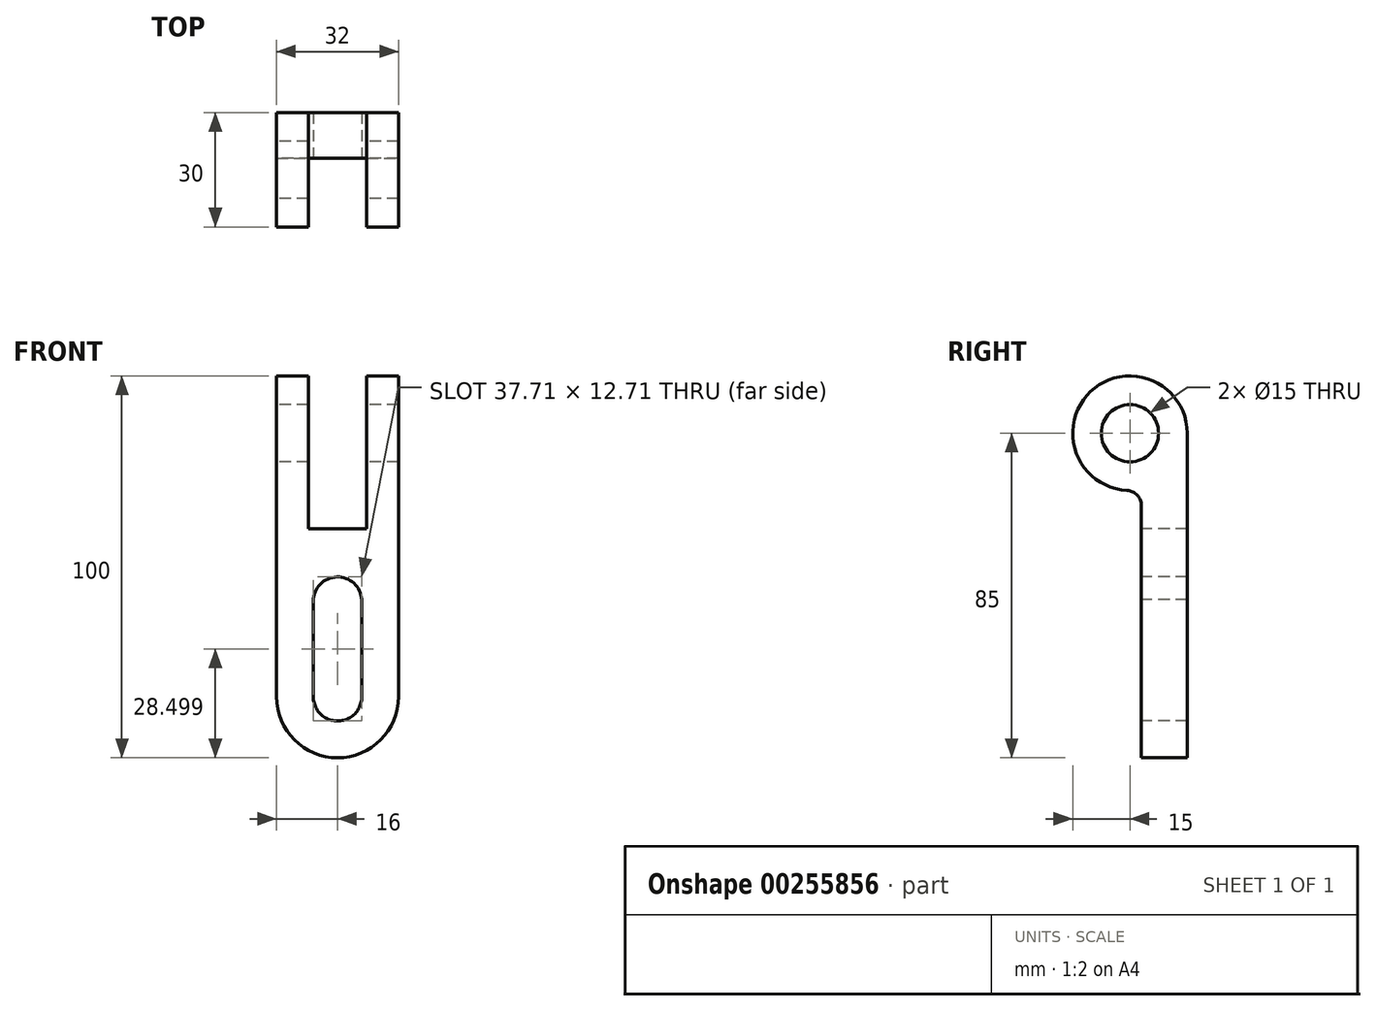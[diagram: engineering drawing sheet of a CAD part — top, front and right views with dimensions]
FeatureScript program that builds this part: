
annotation { "Feature Type Name" : "Feature", "Feature Type Description" : "" }
export const myFeature = defineFeature(function(context is Context, id is Id, definition is map)
    precondition{}
    {
        {
            var Q0;
            Q0=qCreatedBy(makeId("Right.planeOp"),FACE);
            var sketch = newSketch(context, id + "F0", { "sketchPlane" : qUnion([Q0])});
            skCircle(sketch, "E0", {"center": v(0, 0) * mm, "radius": 7.5 * mm});
            skArc(sketch, "E1", {"start": v(15, 0) * mm, "mid": v(-11.62, 9.49) * mm, "end": v(3, -14.7) * mm});
            skLineSegment(sketch, "E2.top", {"start": v(15, -85) * mm, "end": v(3, -85) * mm});
            skLineSegment(sketch, "E2.left", {"start": v(15, 0) * mm, "end": v(15, -85) * mm});
            skLineSegment(sketch, "E2.right", {"start": v(3, -14.7) * mm, "end": v(3, -85) * mm});
            skSolve(sketch);
        }
        {
            var Q0;
            Q0=makeQuery(id+"F0.imprint","IMPRINT",FACE,{"disambiguationData":[TD([[makeQuery(id+"F0.imprint","IMPRINT",EDGE,{"derivedFrom":sQuery(id+"F0.wireOp",EDGE,"E0")}),-1.0]])]});
            extrude(context, id + "F1", {"entities" : qUnion([Q0]), "endBound" : BoundingType.SYMMETRIC, "depth" : 32 * mm});
        }
        {
            var Q0;
            Q0=qCreatedBy(makeId("Front.planeOp"),FACE);
            cPlane(context, id + "F2", {"entities" : qUnion([Q0]), "cplaneType" : CPlaneType.OFFSET, "offset" : 40.5 * mm, "width" : 150 * mm, "height" : 150 * mm});
        }
        {
            var Q0;
            Q0=qCreatedBy(id+"F2.planeOp",FACE);
            var sketch = newSketch(context, id + "F3", { "sketchPlane" : qUnion([Q0])});
            skLineSegment(sketch, "E3.0", {"start": v(16, 15) * mm, "end": v(16, -15) * mm});
            skLineSegment(sketch, "E4.0", {"start": v(-16, 15) * mm, "end": v(-16, -15) * mm});
            skLineSegment(sketch, "E5.0.0", {"start": v(-16, -14.7) * mm, "end": v(-16, -85) * mm});
            skLineSegment(sketch, "E5.0.2", {"start": v(16, -85) * mm, "end": v(16, -14.7) * mm});
            skLineSegment(sketch, "E6.bottom", {"start": v(7.65, -25) * mm, "end": v(-7.65, -25) * mm});
            skLineSegment(sketch, "E6.top", {"start": v(7.65, 25) * mm, "end": v(-7.65, 25) * mm});
            skLineSegment(sketch, "E6.left", {"start": v(7.65, -25) * mm, "end": v(7.65, 25) * mm});
            skLineSegment(sketch, "E6.right", {"start": v(-7.65, -25) * mm, "end": v(-7.65, 25) * mm});
            skPoint(sketch, "E6.middle", {"position": v(0, 0) * mm});
            skArc(sketch, "E7", {"start": v(6.35, -44.37) * mm, "mid": v(0.19, -37.65) * mm, "end": v(-6.36, -44) * mm});
            skArc(sketch, "E8", {"start": v(-6.36, -69) * mm, "mid": v(0, -75.36) * mm, "end": v(6.36, -69) * mm});
            skLineSegment(sketch, "E9", {"start": v(-6.36, -44) * mm, "end": v(-6.36, -69) * mm});
            skLineSegment(sketch, "E10", {"start": v(6.35, -43.62) * mm, "end": v(6.36, -69) * mm});
            skArc(sketch, "E11", {"start": v(-16, -69) * mm, "mid": v(0, -85) * mm, "end": v(16, -69) * mm});
            skLineSegment(sketch, "E12", {"start": v(-16, -85) * mm, "end": v(16, -85) * mm});
            skSolve(sketch);
        }
        {
            var Q0;
            {var subQ0=sQuery(id+"F3.wireOp",EDGE,"Ua7hlya5-Do4J-kOjE-r2rm-KCrWdPRQVA8R");var subQ1=sQuery(id+"F3.wireOp",EDGE,"E5.0.0");var subQ2=makeQuery(id+"F3.imprint","INTERSECT",VERTEX,{"derivedFrom":[subQ1,subQ0]});Q0=makeQuery(id+"F3.imprint","IMPRINT",FACE,{"disambiguationData":[TD([[makeQuery(id+"F3.imprint","IMPRINT",EDGE,{"disambiguationData":[TD([[subQ2,1.0]])],"derivedFrom":subQ1}),1.0]])]});}
            var Q1;
            {var subQ0=sQuery(id+"F3.wireOp",EDGE,"Ua7hlya5-Do4J-kOjE-r2rm-KCrWdPRQVA8R");var subQ1=sQuery(id+"F3.wireOp",EDGE,"E5.0.2");var subQ2=makeQuery(id+"F3.imprint","INTERSECT",VERTEX,{"derivedFrom":[subQ1,subQ0]});Q1=makeQuery(id+"F3.imprint","IMPRINT",FACE,{"disambiguationData":[TD([[makeQuery(id+"F3.imprint","IMPRINT",EDGE,{"disambiguationData":[TD([[subQ2,-1.0]])],"derivedFrom":subQ1}),1.0]])]});}
            var Q2;
            {var subQ5=sQuery(id+"F3.wireOp",EDGE,"E8");Q2=makeQuery(id+"F3.imprint","IMPRINT",FACE,{"disambiguationData":[TD([[makeQuery(id+"F3.imprint","IMPRINT",EDGE,{"derivedFrom":subQ5}),1.0]])]});}
            var Q3;
            Q3=makeQuery(id+"F3.imprint","IMPRINT",FACE,{"disambiguationData":[TD([[makeQuery(id+"F3.imprint","IMPRINT",EDGE,{"derivedFrom":sQuery(id+"F3.wireOp",EDGE,"E6.bottom")}),-1.0]])]});
            extrude(context, id + "F4", {"entities" : qUnion([Q0, Q1, Q2, Q3]), "operationType" : NewBodyOperationType.REMOVE, "endBound" : BoundingType.THROUGH_ALL, "oppositeDirection" : true, "depth" : 25 * mm});
        }
        {
            var Q0;
            {var subQ0=sQuery(id+"F0.wireOp",EDGE,"E2.right");var subQ1=sQuery(id+"F0.wireOp",EDGE,"E1");Q0=makeQuery(id+"F4.boolean.opBoolean","SPLIT",EDGE,{"disambiguationData":[TD([makeQuery(id+"F4.opExtrude","SWEPT_FACE",FACE,{"disambiguationData":[OSD([sQuery(id+"F3.wireOp",EDGE,"E6.right")])]})])],"derivedFrom":makeQuery(id+"F1.opExtrude","SWEPT_EDGE",EDGE,{"disambiguationData":[OSD([subQ1,subQ0])]})});}
            var Q1;
            {var subQ0=sQuery(id+"F0.wireOp",EDGE,"E2.right");var subQ1=sQuery(id+"F0.wireOp",EDGE,"E1");Q1=makeQuery(id+"F4.boolean.opBoolean","SPLIT",EDGE,{"disambiguationData":[TD([makeQuery(id+"F4.opExtrude","SWEPT_FACE",FACE,{"disambiguationData":[OSD([sQuery(id+"F3.wireOp",EDGE,"E6.left")])]})])],"derivedFrom":makeQuery(id+"F1.opExtrude","SWEPT_EDGE",EDGE,{"disambiguationData":[OSD([subQ1,subQ0])]})});}
            fillet(context, id + "F5", {"entities" : qUnion([Q0, Q1]), "radius" : 4 * mm, "tangentPropagation" : true, "allowEdgeOverflow" : false});
        }
        {
            var Q0;
            {var subQ0=sQuery(id+"F3.wireOp",EDGE,"E12");var subQ1=sQuery(id+"F3.wireOp",EDGE,"E5.0.0");var subQ2=makeQuery(id+"F3.imprint","INTERSECT",VERTEX,{"derivedFrom":[subQ1,subQ0]});Q0=makeQuery(id+"F3.imprint","IMPRINT",FACE,{"disambiguationData":[TD([[makeQuery(id+"F3.imprint","IMPRINT",EDGE,{"disambiguationData":[TD([[subQ2,1.0]])],"derivedFrom":subQ1}),1.0]])]});}
            var Q1;
            {var subQ0=sQuery(id+"F3.wireOp",EDGE,"E12");var subQ1=sQuery(id+"F3.wireOp",EDGE,"E5.0.2");var subQ2=makeQuery(id+"F3.imprint","INTERSECT",VERTEX,{"derivedFrom":[subQ1,subQ0]});Q1=makeQuery(id+"F3.imprint","IMPRINT",FACE,{"disambiguationData":[TD([[makeQuery(id+"F3.imprint","IMPRINT",EDGE,{"disambiguationData":[TD([[subQ2,-1.0]])],"derivedFrom":subQ1}),1.0]])]});}
            var Q2;
            {var subQ5=sQuery(id+"F3.wireOp",EDGE,"E8");Q2=makeQuery(id+"F3.imprint","IMPRINT",FACE,{"disambiguationData":[TD([[makeQuery(id+"F3.imprint","IMPRINT",EDGE,{"derivedFrom":subQ5}),1.0]])]});}
            var Q3;
            Q3=makeQuery(id+"F3.imprint","IMPRINT",FACE,{"disambiguationData":[TD([[makeQuery(id+"F3.imprint","IMPRINT",EDGE,{"derivedFrom":sQuery(id+"F3.wireOp",EDGE,"E6.bottom")}),-1.0]])]});
            extrude(context, id + "F6", {"entities" : qUnion([Q0, Q1, Q2, Q3]), "operationType" : NewBodyOperationType.REMOVE, "endBound" : BoundingType.THROUGH_ALL, "oppositeDirection" : true, "depth" : 25 * mm});
        }
    });
